# Revit family: plfy-ep22_160emg8_60Hz
name_source: partatom
category: 機械設備
units: mm (PartAtom-declared; Revit-internal decimal feet)

## family parameters
OmniClass タイトル = Split System Air Conditioning Units
OmniClass 番号 = 23.75.10.24.21.27.27
パーツ タイプ = 標準
ロード時にボイドで切り取り = いいえ
丸型コネクタ寸法 = 直径を使用
作業面ベース = いいえ
共有 = いいえ
常に垂直 = はい
部屋計算ポイント = はい

## types (11) — shared parameters
Clearance Back = 1500  [stored 4.92126 ft]
Clearance Bottom = 1000  [stored 3.28084 ft]
Clearance Front = 1500  [stored 4.92126 ft]
Clearance Left = 1500  [stored 4.92126 ft]
Clearance Right = 1500  [stored 4.92126 ft]
Depth = 840  [stored 2.75591 ft]
IfcExportAs = IfcUnitaryEquipmentType
IfcExportType = AIRCONDITIONINGUNIT
OmniClassCode = 23-33 17 13 11
Panel Depth = 950  [stored 3.1168 ft]
Panel Height = 40  [stored 0.131234 ft]
Panel Width = 950  [stored 3.1168 ft]
URL = https://www.mitsubishielectric.co.jp
Uniclass2015Code = Pr_70_65_03_84
Uniclass2015Title = Split coil remote air cooled condensing units
Uniclass2015Version = Systems v1.9
Width = 840  [stored 2.75591 ft]
ケーブルサイズ = 0 mm
サービススペース = はい
ドレン管径 = 25 mm
ドレン管径(外径) = 32 mm
ドレン管高さ = 190
パネルマテリアル = <カテゴリ別>
仕様書バージョン = Version1.0
企業コード = 108420
冷媒ガス管高さ = 170  [stored 0.557743 ft]
冷媒液管高さ = 140  [stored 0.459318 ft]
冷媒管径 = 100 mm
分類コード = 50053003123030
参照している仕様書等のバージョン = 公共建築物標準仕様書（機械設備工事編）平成31年度版
吊りボルト_H = 105  [stored 0.344488 ft]
吊り位置X = 795  [stored 2.60827 ft]
吊り位置Y = 660
周波数 = 60 Hz
呼称 = 室内機_カセット形 (4方向吹出形)
始動方式 = 直入
形式 = カセット形 (4方向吹出形)
推奨ブレーカー容量 = 0 A
本体マテリアル = <カテゴリ別>
極数 = 1
法定耐用年数 = 6
消費電力 = 0 kW
消費電力_冷房 = 0 kW
消費電力_加湿器 = 0 kW
消費電力_暖房 = 0 kW
消費電力_電気ヒーター = 0 kW
発停方法 = 付属スイッチ
相 = 1
積算_科目 = 1 空気調和設備
符号 = PAC_CK4
製品リリース年月 = 2021年5月10日
製品出荷対象 = 国内
製造元 = 三菱電機株式会社
設置方法 = カセット形
説明 = ビル用マルチ 天井カセット形(4方向吹出)室内機
負荷分類 = 3_ファン類
運転質量 = 0.00 kg
電動機出力_送風機 = 0 kW
電圧 = 200 V
電源_H = 37
zero-valued in all types: 価格, 有効加湿量

## per-type parameters (varying)
- 天井4方向_PLFY-EP22EMG8: Clearance Top=265  [stored 0.869423 ft]; Height=258  [stored 0.846457 ft]; MAX風量=900.0 m³/h; MID風量=840.0 m³/h; MID風量2=780.0 m³/h; MIN風量=720.0 m³/h; 冷媒ガス管径=12.7 mm; 冷媒ガス管長さ=76.5  [stored 0.250984 ft]; 冷媒液管径=6.35 mm; 冷媒液管長さ=76  [stored 0.249344 ft]; 冷媒管径符号=Ac; 冷房能力=2 kW; 暖房能力=3 kW; 構成品番=PLFY-EP22EMG; 製品質量=25.00 kg; 質量=30.00 kg; 音響パワーレベル(dB)=43; 音響パワーレベルMID1 (dB)=42; 音響パワーレベルMID2 (dB)=41; 音響パワーレベルMIN=39; 風量=900.0 m³/h; 風量（中）（m3／min）=14; 風量（弱）（m3／min）=13; 風量（強）（m3／min）=15; 風量（静）（m3／min）=12
- 天井4方向_PLFY-EP56EMG8: Clearance Top=265  [stored 0.869423 ft]; Height=258  [stored 0.846457 ft]; MAX風量=1020.0 m³/h; MID風量=900.0 m³/h; MID風量2=840.0 m³/h; MIN風量=780.0 m³/h; 冷媒ガス管径=12.7 mm; 冷媒ガス管長さ=76.5  [stored 0.250984 ft]; 冷媒液管径=6.35 mm; 冷媒液管長さ=76  [stored 0.249344 ft]; 冷媒管径符号=Ac; 冷房能力=6 kW; 暖房能力=6 kW; 構成品番=PLFY-EP56EMG; 製品質量=26.00 kg; 質量=31.20 kg; 音響パワーレベル(dB)=49; 音響パワーレベルMID1 (dB)=48; 音響パワーレベルMID2 (dB)=47; 音響パワーレベルMIN=46; 風量=1020.0 m³/h; 風量（中）（m3／min）=15; 風量（弱）（m3／min）=14; 風量（強）（m3／min）=17; 風量（静）（m3／min）=13
- 天井4方向_PLFY-EP71EMG8: Clearance Top=265  [stored 0.869423 ft]; Height=258  [stored 0.846457 ft]; MAX風量=1500.0 m³/h; MID風量=1260.0 m³/h; MID風量2=1020.0 m³/h; MIN風量=840.0 m³/h; 冷媒ガス管径=15.88 mm; 冷媒ガス管長さ=79.5  [stored 0.260827 ft]; 冷媒液管径=9.52 mm; 冷媒液管長さ=79.5  [stored 0.260827 ft]; 冷媒管径符号=Bd; 冷房能力=7 kW; 暖房能力=8 kW; 構成品番=PLFY-EP71EMG; 製品質量=26.00 kg; 質量=31.20 kg; 音響パワーレベル(dB)=54; 音響パワーレベルMID1 (dB)=52; 音響パワーレベルMID2 (dB)=50; 音響パワーレベルMIN=48; 風量=1500.0 m³/h; 風量（中）（m3／min）=21; 風量（弱）（m3／min）=17; 風量（強）（m3／min）=25; 風量（静）（m3／min）=14
- 天井4方向_PLFY-EP112EMG8: Clearance Top=305  [stored 1.00066 ft]; Height=298  [stored 0.97769 ft]; MAX風量=2160.0 m³/h; MID風量=1920.0 m³/h; MID風量2=1620.0 m³/h; MIN風量=1260.0 m³/h; 冷媒ガス管径=15.88 mm; 冷媒ガス管長さ=79.5  [stored 0.260827 ft]; 冷媒液管径=9.52 mm; 冷媒液管長さ=79.5  [stored 0.260827 ft]; 冷媒管径符号=Bd; 冷房能力=11 kW; 暖房能力=13 kW; 構成品番=PLFY-EP112EMG; 製品質量=32.00 kg; 質量=38.40 kg; 音響パワーレベル(dB)=61; 音響パワーレベルMID1 (dB)=58; 音響パワーレベルMID2 (dB)=56; 音響パワーレベルMIN=53; 風量=2160.0 m³/h; 風量（中）（m3／min）=32; 風量（弱）（m3／min）=27; 風量（強）（m3／min）=36; 風量（静）（m3／min）=21
- 天井4方向_PLFY-EP140EMG8: Clearance Top=305  [stored 1.00066 ft]; Height=298  [stored 0.97769 ft]; MAX風量=2160.0 m³/h; MID風量=1920.0 m³/h; MID風量2=1620.0 m³/h; MIN風量=1320.0 m³/h; 冷媒ガス管径=15.88 mm; 冷媒ガス管長さ=79.5  [stored 0.260827 ft]; 冷媒液管径=9.52 mm; 冷媒液管長さ=79.5  [stored 0.260827 ft]; 冷媒管径符号=Bd; 冷房能力=14 kW; 暖房能力=16 kW; 構成品番=PLFY-EP140EMG; 製品質量=32.00 kg; 質量=38.40 kg; 音響パワーレベル(dB)=62; 音響パワーレベルMID1 (dB)=59; 音響パワーレベルMID2 (dB)=57; 音響パワーレベルMIN=55; 風量=2160.0 m³/h; 風量（中）（m3／min）=32; 風量（弱）（m3／min）=27; 風量（強）（m3／min）=36; 風量（静）（m3／min）=22
- 天井4方向_PLFY-EP160EMG8: Clearance Top=305  [stored 1.00066 ft]; Height=298  [stored 0.97769 ft]; MAX風量=2160.0 m³/h; MID風量=1920.0 m³/h; MID風量2=1620.0 m³/h; MIN風量=1380.0 m³/h; 冷媒ガス管径=15.88 mm; 冷媒ガス管長さ=79.5  [stored 0.260827 ft]; 冷媒液管径=9.52 mm; 冷媒液管長さ=79.5  [stored 0.260827 ft]; 冷媒管径符号=Bd; 冷房能力=16 kW; 暖房能力=18 kW; 構成品番=PLFY-EP160EMG; 製品質量=32.00 kg; 質量=38.40 kg; 音響パワーレベル(dB)=62; 音響パワーレベルMID1 (dB)=59; 音響パワーレベルMID2 (dB)=57; 音響パワーレベルMIN=56; 風量=2160.0 m³/h; 風量（中）（m3／min）=32; 風量（弱）（m3／min）=27; 風量（強）（m3／min）=36; 風量（静）（m3／min）=23
- 天井4方向_PLFY-EP45EMG8: Clearance Top=265  [stored 0.869423 ft]; Height=258  [stored 0.846457 ft]; MAX風量=1020.0 m³/h; MID風量=900.0 m³/h; MID風量2=840.0 m³/h; MIN風量=780.0 m³/h; 冷媒ガス管径=12.7 mm; 冷媒ガス管長さ=76.5  [stored 0.250984 ft]; 冷媒液管径=6.35 mm; 冷媒液管長さ=76  [stored 0.249344 ft]; 冷媒管径符号=Ac; 冷房能力=5 kW; 暖房能力=5 kW; 構成品番=PLFY-EP45EMG; 製品質量=26.00 kg; 質量=31.20 kg; 音響パワーレベル(dB)=48; 音響パワーレベルMID1 (dB)=47; 音響パワーレベルMID2 (dB)=45; 音響パワーレベルMIN=44; 風量=1020.0 m³/h; 風量（中）（m3／min）=15; 風量（弱）（m3／min）=14; 風量（強）（m3／min）=17; 風量（静）（m3／min）=13
- 天井4方向_PLFY-EP28EMG8: Clearance Top=265  [stored 0.869423 ft]; Height=258  [stored 0.846457 ft]; MAX風量=900.0 m³/h; MID風量=840.0 m³/h; MID風量2=780.0 m³/h; MIN風量=720.0 m³/h; 冷媒ガス管径=12.7 mm; 冷媒ガス管長さ=76.5  [stored 0.250984 ft]; 冷媒液管径=6.35 mm; 冷媒液管長さ=76  [stored 0.249344 ft]; 冷媒管径符号=Ac; 冷房能力=3 kW; 暖房能力=3 kW; 構成品番=PLFY-EP28EMG; 製品質量=25.00 kg; 質量=30.00 kg; 音響パワーレベル(dB)=43; 音響パワーレベルMID1 (dB)=42; 音響パワーレベルMID2 (dB)=41; 音響パワーレベルMIN=39; 風量=900.0 m³/h; 風量（中）（m3／min）=14; 風量（弱）（m3／min）=13; 風量（強）（m3／min）=15; 風量（静）（m3／min）=12
- 天井4方向_PLFY-EP36EMG8: Clearance Top=265  [stored 0.869423 ft]; Height=258  [stored 0.846457 ft]; MAX風量=1020.0 m³/h; MID風量=900.0 m³/h; MID風量2=840.0 m³/h; MIN風量=780.0 m³/h; 冷媒ガス管径=12.7 mm; 冷媒ガス管長さ=76.5  [stored 0.250984 ft]; 冷媒液管径=6.35 mm; 冷媒液管長さ=76  [stored 0.249344 ft]; 冷媒管径符号=Ac; 冷房能力=4 kW; 暖房能力=4 kW; 構成品番=PLFY-EP36EMG; 製品質量=25.00 kg; 質量=30.00 kg; 音響パワーレベル(dB)=46; 音響パワーレベルMID1 (dB)=45; 音響パワーレベルMID2 (dB)=43; 音響パワーレベルMIN=42; 風量=1020.0 m³/h; 風量（中）（m3／min）=15; 風量（弱）（m3／min）=14; 風量（強）（m3／min）=17; 風量（静）（m3／min）=13
- 天井4方向_PLFY-EP80EMG8: Clearance Top=305  [stored 1.00066 ft]; Height=298  [stored 0.97769 ft]; MAX風量=1620.0 m³/h; MID風量=1380.0 m³/h; MID風量2=1200.0 m³/h; MIN風量=1020.0 m³/h; 冷媒ガス管径=15.88 mm; 冷媒ガス管長さ=79.5  [stored 0.260827 ft]; 冷媒液管径=9.52 mm; 冷媒液管長さ=79.5  [stored 0.260827 ft]; 冷媒管径符号=Bd; 冷房能力=8 kW; 暖房能力=9 kW; 構成品番=PLFY-EP80EMG; 製品質量=30.00 kg; 質量=36.00 kg; 音響パワーレベル(dB)=54; 音響パワーレベルMID1 (dB)=52; 音響パワーレベルMID2 (dB)=51; 音響パワーレベルMIN=50; 風量=1620.0 m³/h; 風量（中）（m3／min）=23; 風量（弱）（m3／min）=20; 風量（強）（m3／min）=27; 風量（静）（m3／min）=17
- 天井4方向_PLFY-EP90EMG8: Clearance Top=305  [stored 1.00066 ft]; Height=298  [stored 0.97769 ft]; MAX風量=1620.0 m³/h; MID風量=1380.0 m³/h; MID風量2=1200.0 m³/h; MIN風量=1020.0 m³/h; 冷媒ガス管径=15.88 mm; 冷媒ガス管長さ=79.5  [stored 0.260827 ft]; 冷媒液管径=9.52 mm; 冷媒液管長さ=79.5  [stored 0.260827 ft]; 冷媒管径符号=Bd; 冷房能力=9 kW; 暖房能力=10 kW; 構成品番=PLFY-EP90EMG; 製品質量=30.00 kg; 質量=36.00 kg; 音響パワーレベル(dB)=54; 音響パワーレベルMID1 (dB)=52; 音響パワーレベルMID2 (dB)=51; 音響パワーレベルMIN=50; 風量=1620.0 m³/h; 風量（中）（m3／min）=23; 風量（弱）（m3／min）=20; 風量（強）（m3／min）=27; 風量（静）（m3／min）=17

note: [stored X ft] marks values corroborated as IEEE doubles in the binary element streams (Revit-internal decimal feet)

## geometry (parser evidence)
native form markers: Blend x16
no freeform markers — native parametric forms only
